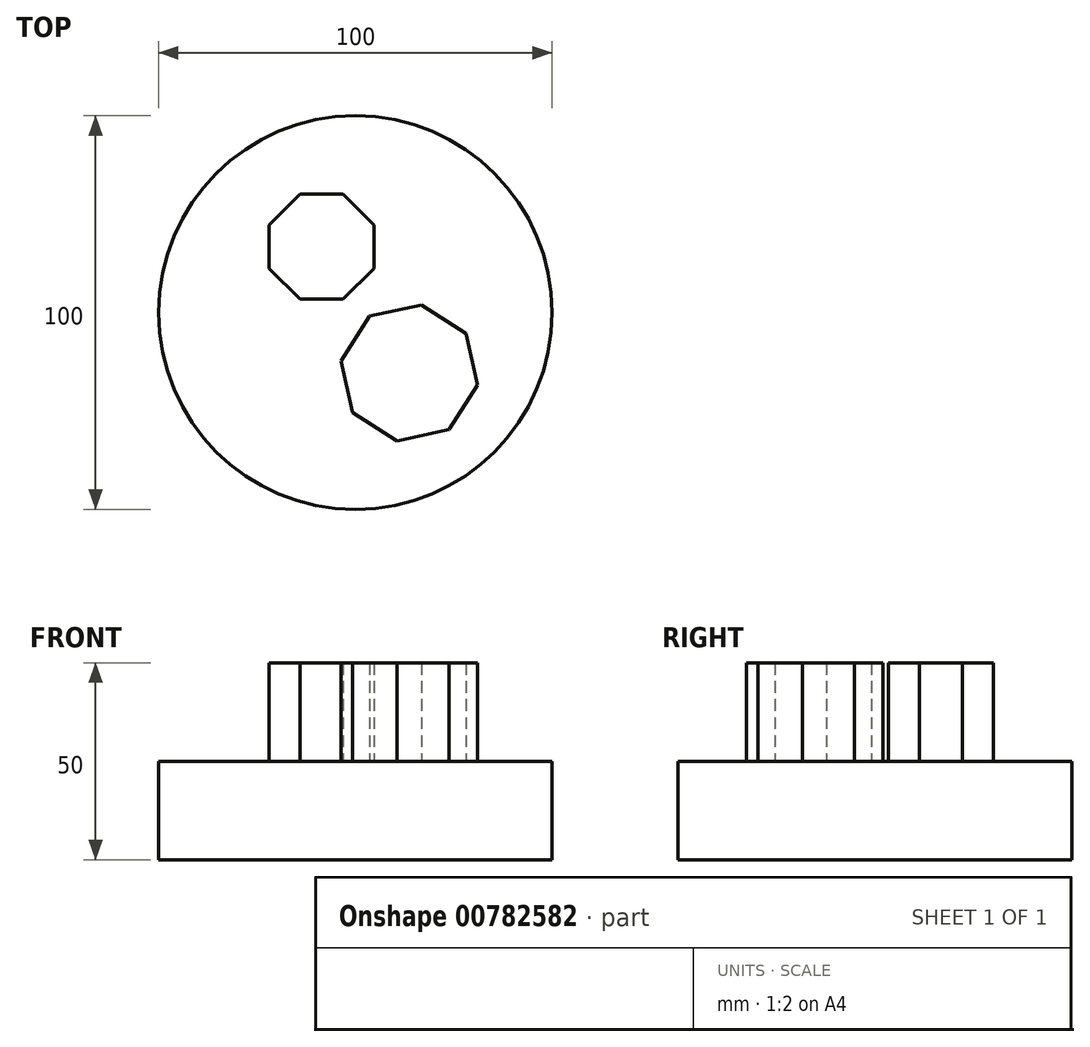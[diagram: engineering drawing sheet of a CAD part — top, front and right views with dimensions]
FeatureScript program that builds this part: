
annotation { "Feature Type Name" : "Feature", "Feature Type Description" : "" }
export const myFeature = defineFeature(function(context is Context, id is Id, definition is map)
    precondition{}
    {
        {
            var Q0;
            Q0=qCreatedBy(makeId("Top.planeOp"),FACE);
            var sketch = newSketch(context, id + "F0", { "sketchPlane" : qUnion([Q0])});
            skCircle(sketch, "E0", {"center": v(0, 0) * mm, "radius": 50 * mm});
            skSolve(sketch);
        }
        {
            var Q0;
            Q0=makeQuery(id+"F0.imprint","IMPRINT",FACE,{"disambiguationData":[TD([[makeQuery(id+"F0.imprint","IMPRINT",EDGE,{"derivedFrom":sQuery(id+"F0.wireOp",EDGE,"E0")}),1.0]])]});
            extrude(context, id + "F1", {"entities" : qUnion([Q0]), "depth" : 25 * mm, "offsetDistance" : 25 * mm});
        }
        {
            var Q0;
            Q0=makeQuery(id+"F1.opExtrude","CAP_FACE",FACE,{"disambiguationData":[OSD([sQuery(id+"F0.wireOp",EDGE,"E0")])],"isStart":false});
            var sketch = newSketch(context, id + "F2", { "sketchPlane" : qUnion([Q0])});
            skCircle(sketch, "E1.cCircle", {"center": v(13.7, -15.34) * mm, "radius": 16.25 * mm, "construction": true});
            skLineSegment(sketch, "E1.0", {"start": v(-3.62, -12.27) * mm, "end": v(3.62, -0.92) * mm});
            skLineSegment(sketch, "E1.1", {"start": v(3.62, -0.92) * mm, "end": v(16.76, 1.98) * mm});
            skLineSegment(sketch, "E1.2", {"start": v(16.76, 1.98) * mm, "end": v(28.11, -5.25) * mm});
            skLineSegment(sketch, "E1.3", {"start": v(28.11, -5.25) * mm, "end": v(31.02, -18.4) * mm});
            skLineSegment(sketch, "E1.4", {"start": v(31.02, -18.4) * mm, "end": v(23.78, -29.75) * mm});
            skLineSegment(sketch, "E1.5", {"start": v(23.78, -29.75) * mm, "end": v(10.64, -32.66) * mm});
            skLineSegment(sketch, "E1.6", {"start": v(10.64, -32.66) * mm, "end": v(-0.71, -25.42) * mm});
            skLineSegment(sketch, "E1.7", {"start": v(-0.71, -25.42) * mm, "end": v(-3.62, -12.27) * mm});
            skPoint(sketch, "E1.0.midPoint", {"position": v(0, -6.6) * mm});
            skCircle(sketch, "E2.cCircle", {"center": v(-8.59, 16.76) * mm, "radius": 13.32 * mm, "construction": true});
            skLineSegment(sketch, "E2.0", {"start": v(-14.1, 30.08) * mm, "end": v(-3.07, 30.08) * mm});
            skLineSegment(sketch, "E2.1", {"start": v(-3.07, 30.08) * mm, "end": v(4.73, 22.28) * mm});
            skLineSegment(sketch, "E2.2", {"start": v(4.73, 22.28) * mm, "end": v(4.73, 11.25) * mm});
            skLineSegment(sketch, "E2.3", {"start": v(4.73, 11.25) * mm, "end": v(-3.07, 3.45) * mm});
            skLineSegment(sketch, "E2.4", {"start": v(-3.07, 3.45) * mm, "end": v(-14.1, 3.45) * mm});
            skLineSegment(sketch, "E2.5", {"start": v(-14.1, 3.45) * mm, "end": v(-21.9, 11.25) * mm});
            skLineSegment(sketch, "E2.6", {"start": v(-21.9, 11.25) * mm, "end": v(-21.9, 22.28) * mm});
            skLineSegment(sketch, "E2.7", {"start": v(-21.9, 22.28) * mm, "end": v(-14.1, 30.08) * mm});
            skPoint(sketch, "E2.0.midPoint", {"position": v(-8.59, 30.08) * mm});
            skSolve(sketch);
        }
        {
            var Q0;
            Q0 = qSketchRegion(id + "F2", true);
            extrude(context, id + "F3", {"entities" : qUnion([Q0]), "operationType" : NewBodyOperationType.ADD, "depth" : 25 * mm, "offsetDistance" : 25 * mm});
        }
    });
